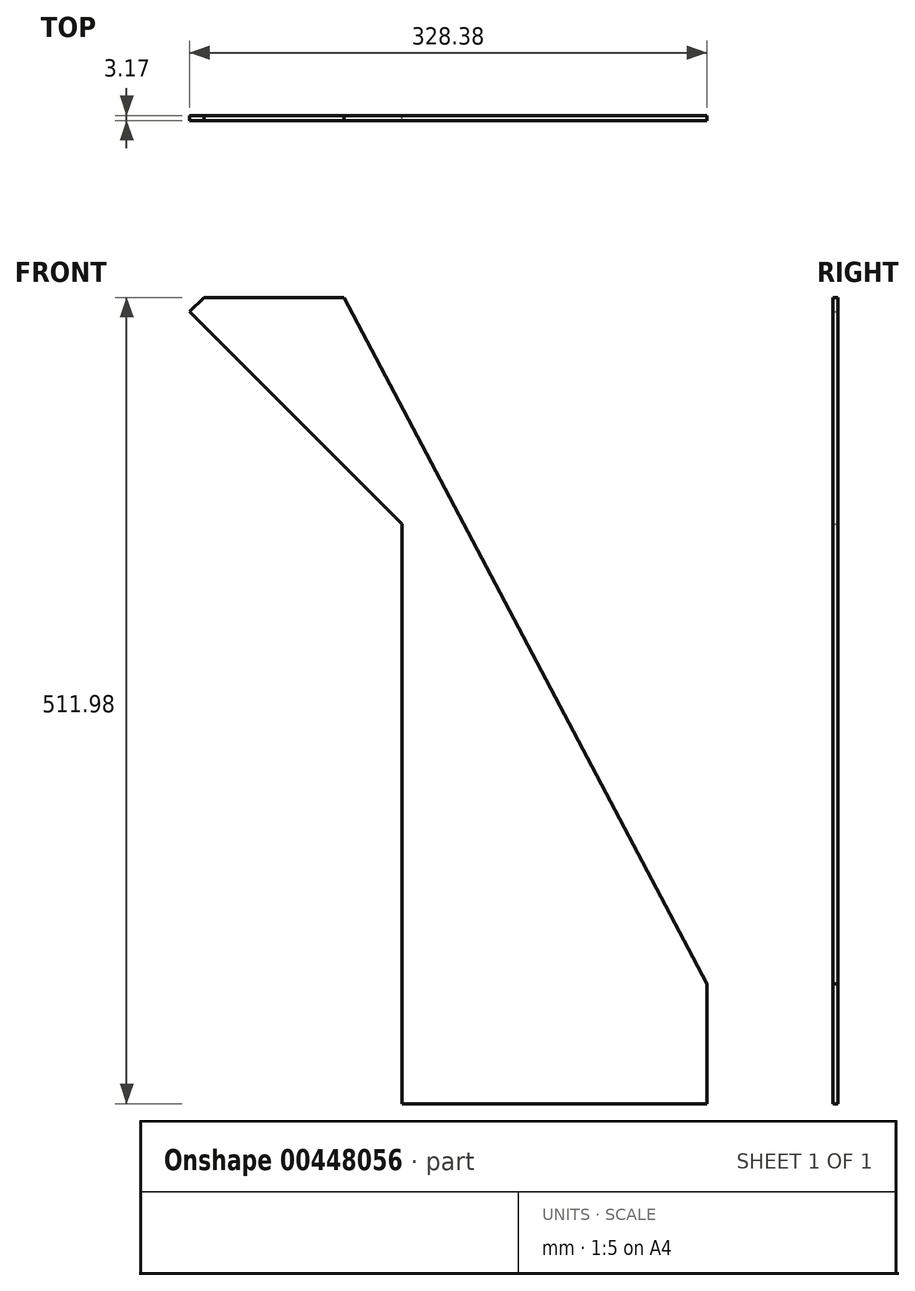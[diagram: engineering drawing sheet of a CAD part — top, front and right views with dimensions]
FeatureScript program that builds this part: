
annotation { "Feature Type Name" : "Feature", "Feature Type Description" : "" }
export const myFeature = defineFeature(function(context is Context, id is Id, definition is map)
    precondition{}
    {
        {
            var Q0;
            Q0=qCreatedBy(makeId("Front.planeOp"),FACE);
            var sketch = newSketch(context, id + "F0", { "sketchPlane" : qUnion([Q0])});
            skLineSegment(sketch, "E0", {"start": v(0, 0) * mm, "end": v(193.68, 0) * mm});
            skLineSegment(sketch, "E1", {"start": v(0, 0) * mm, "end": v(0, 368.3) * mm});
            skLineSegment(sketch, "E2", {"start": v(193.68, 0) * mm, "end": v(193.68, 76.2) * mm});
            skLineSegment(sketch, "E3", {"start": v(0, 368.3) * mm, "end": v(-134.7, 503) * mm});
            skLineSegment(sketch, "E4", {"start": v(-134.7, 503) * mm, "end": v(-125.72, 511.98) * mm});
            skLineSegment(sketch, "E5", {"start": v(8.98, 377.28) * mm, "end": v(0, 368.3) * mm});
            skLineSegment(sketch, "E6", {"start": v(-125.72, 511.98) * mm, "end": v(-36.82, 511.98) * mm});
            skLineSegment(sketch, "E7", {"start": v(-36.82, 511.98) * mm, "end": v(193.68, 76.2) * mm});
            skSolve(sketch);
        }
        {
            var Q0;
            Q0=makeQuery(id+"F0.imprint","IMPRINT",FACE,{"disambiguationData":[TD([[makeQuery(id+"F0.imprint","IMPRINT",EDGE,{"derivedFrom":sQuery(id+"F0.wireOp",EDGE,"E0")}),1.0]])]});
            extrude(context, id + "F1", {"entities" : qUnion([Q0]), "depth" : 3.17 * mm});
        }
    });
